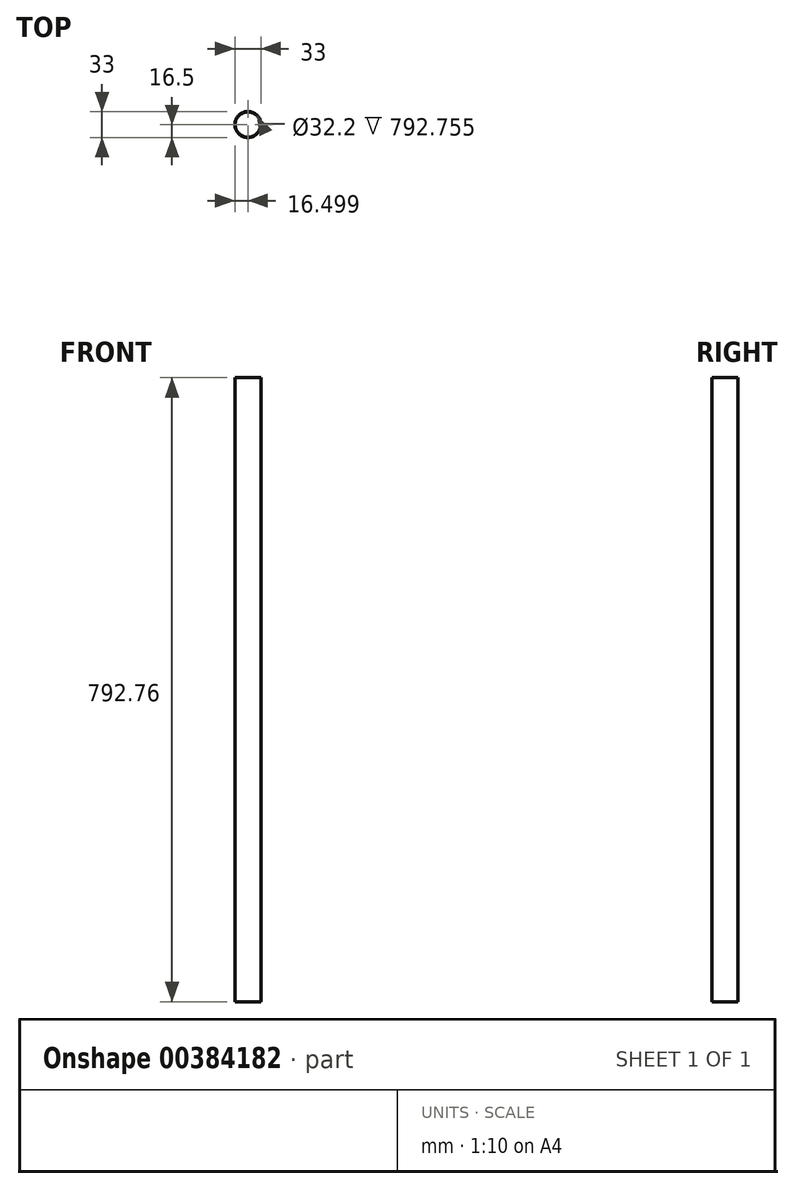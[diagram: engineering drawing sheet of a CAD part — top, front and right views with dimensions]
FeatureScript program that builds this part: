
annotation { "Feature Type Name" : "Feature", "Feature Type Description" : "" }
export const myFeature = defineFeature(function(context is Context, id is Id, definition is map)
    precondition{}
    {
        {
            var Q0;
            Q0=qCreatedBy(makeId("Front.planeOp"),FACE);
            var sketch = newSketch(context, id + "F0", { "sketchPlane" : qUnion([Q0])});
            skLineSegment(sketch, "E0.bottom", {"start": v(-1.18, 259.3) * mm, "end": v(15.32, 259.3) * mm});
            skLineSegment(sketch, "E0.top", {"start": v(-1.18, -533.45) * mm, "end": v(15.32, -533.45) * mm});
            skLineSegment(sketch, "E0.left", {"start": v(-1.18, 259.3) * mm, "end": v(-1.18, -533.45) * mm});
            skLineSegment(sketch, "E0.right", {"start": v(15.32, 259.3) * mm, "end": v(15.32, -533.45) * mm});
            skSolve(sketch);
        }
        {
            var Q0;
            Q0=makeQuery(id+"F0.imprint","IMPRINT",FACE,{"disambiguationData":[TD([[makeQuery(id+"F0.imprint","IMPRINT",EDGE,{"derivedFrom":sQuery(id+"F0.wireOp",EDGE,"E0.bottom")}),-1.0]])]});
            var Q1;
            Q1=sQuery(id+"F0.wireOp",EDGE,"E0.left");
            revolve(context, id + "F1", {"entities" : qUnion([Q0]), "axis" : qUnion([Q1]), "revolveType" : RevolveType.FULL});
        }
        {
            var Q0;
            Q0=makeQuery(id+"F1.opRevolve","SWEPT_FACE",FACE,{"disambiguationData":[OSD([sQuery(id+"F0.wireOp",EDGE,"E0.bottom")])]});
            var sketch = newSketch(context, id + "F2", { "sketchPlane" : qUnion([Q0])});
            skCircle(sketch, "E1", {"center": v(-1.18, 0) * mm, "radius": 16.1 * mm});
            skSolve(sketch);
        }
        {
            var Q0;
            Q0=sQuery(id+"F2.wireOp",VERTEX,"E1.center");
            var Q1;
            Q1=makeQuery(id+"F1.opRevolve","SWEPT_BODY",BODY,{"disambiguationData":[OSD([sQuery(id+"F0.wireOp",EDGE,"E0.bottom"),sQuery(id+"F0.wireOp",EDGE,"E0.top"),sQuery(id+"F0.wireOp",EDGE,"E0.left"),sQuery(id+"F0.wireOp",EDGE,"E0.right")])]});
            hole(context, id + "F3", {"style" : HoleStyle.SIMPLE, "endStyle" : HoleEndStyle.BLIND, "holeDiameter" : 32.2 * mm, "holeDepth" : 800 * mm, "isTappedThrough" : true, "tappedDepth" : 12 * mm, "tapClearance" : 3, "locations" : qUnion([Q0]), "scope" : qUnion([Q1])});
        }
    });
